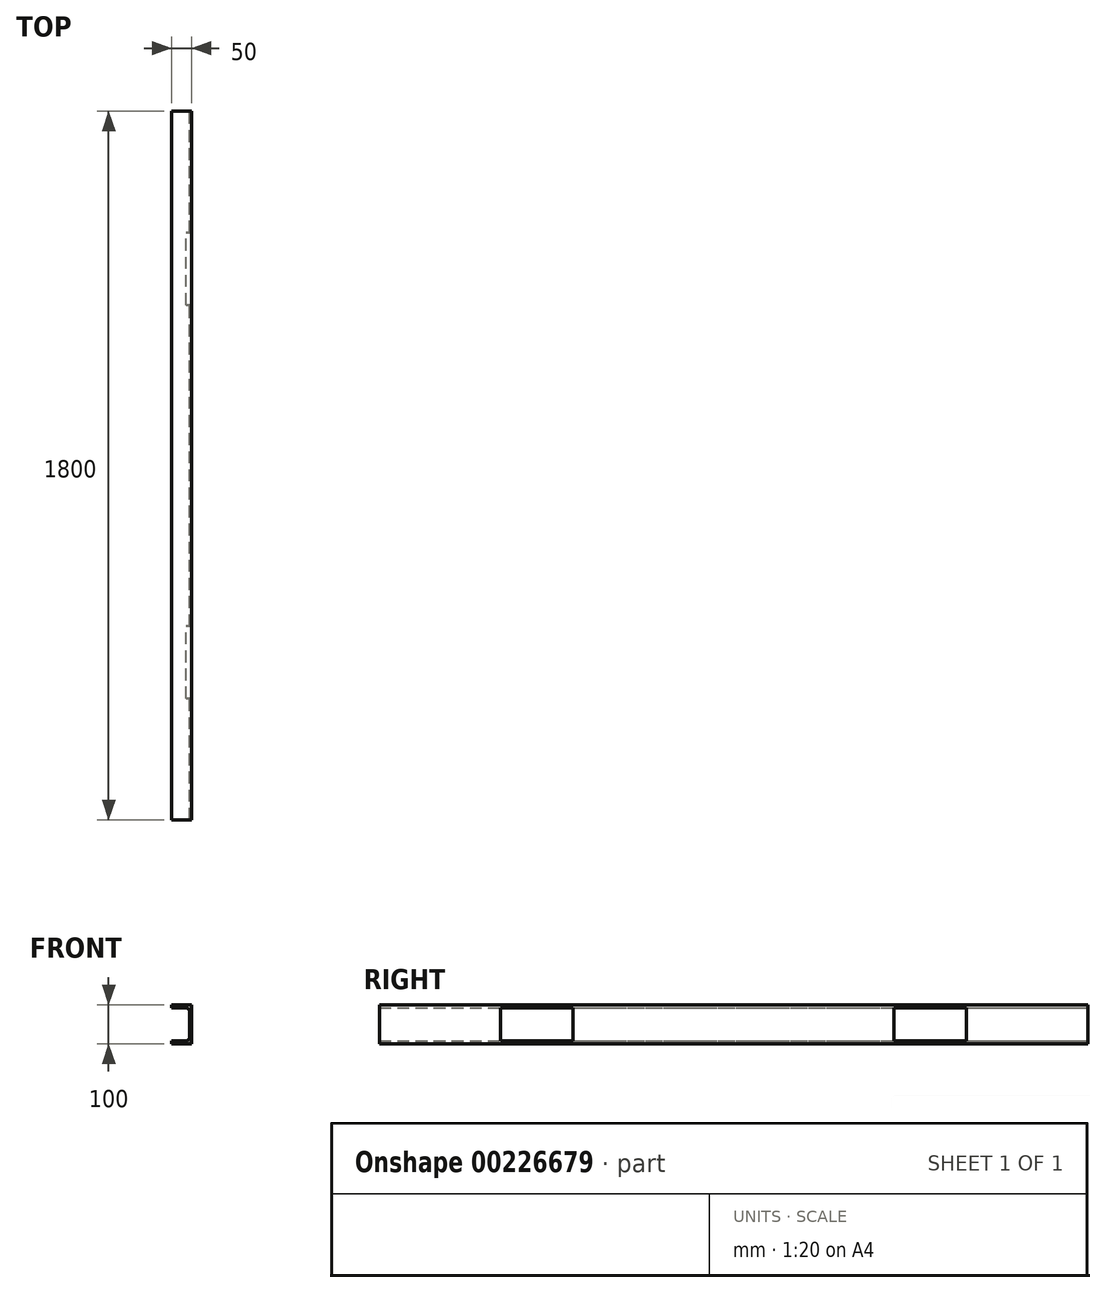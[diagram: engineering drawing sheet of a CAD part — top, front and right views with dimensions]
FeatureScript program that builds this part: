
annotation { "Feature Type Name" : "Feature", "Feature Type Description" : "" }
export const myFeature = defineFeature(function(context is Context, id is Id, definition is map)
    precondition{}
    {
        {
            var Q0;
            Q0=qCreatedBy(makeId("Front.planeOp"),FACE);
            var sketch = newSketch(context, id + "F0", { "sketchPlane" : qUnion([Q0])});
            skLineSegment(sketch, "E0", {"start": v(-50, 50) * mm, "end": v(0, 50) * mm});
            skLineSegment(sketch, "E1", {"start": v(0, 50) * mm, "end": v(0, -50) * mm});
            skLineSegment(sketch, "E2", {"start": v(0, -50) * mm, "end": v(-50, -50) * mm});
            skLineSegment(sketch, "E3", {"start": v(-50, -50) * mm, "end": v(-50, -41.5) * mm});
            skLineSegment(sketch, "E4", {"start": v(-50, -41.5) * mm, "end": v(-14, -41.5) * mm});
            skLineSegment(sketch, "E5", {"start": v(-50, 50) * mm, "end": v(-50, 41.5) * mm});
            skLineSegment(sketch, "E6", {"start": v(-50, 41.5) * mm, "end": v(-14, 41.5) * mm});
            skLineSegment(sketch, "E7", {"start": v(-5, 32.5) * mm, "end": v(-5, -32.5) * mm});
            skPoint(sketch, "E8.visualSharp", {"position": v(-5, 41.5) * mm});
            skArc(sketch, "E8.filletArc", {"start": v(-5, 32.5) * mm, "mid": v(-7.64, 38.86) * mm, "end": v(-14, 41.5) * mm});
            skPoint(sketch, "E9.visualSharp", {"position": v(-5, -41.5) * mm});
            skArc(sketch, "E9.filletArc", {"start": v(-14, -41.5) * mm, "mid": v(-7.64, -38.86) * mm, "end": v(-5, -32.5) * mm});
            skSolve(sketch);
        }
        {
            var Q0;
            Q0=makeQuery(id+"F0.imprint","IMPRINT",FACE,{"disambiguationData":[TD([[makeQuery(id+"F0.imprint","IMPRINT",EDGE,{"derivedFrom":sQuery(id+"F0.wireOp",EDGE,"E0")}),-1.0]])]});
            extrude(context, id + "F1", {"entities" : qUnion([Q0]), "depth" : 1800 * mm});
        }
        {
            var Q0;
            Q0=qCreatedBy(makeId("Right.planeOp"),FACE);
            var sketch = newSketch(context, id + "F2", { "sketchPlane" : qUnion([Q0])});
            skLineSegment(sketch, "E10.top", {"start": v(-308, 42) * mm, "end": v(-461.92, 42) * mm});
            skLineSegment(sketch, "E10.left", {"start": v(-308, 0) * mm, "end": v(-308, 42) * mm});
            skLineSegment(sketch, "E11.bottom", {"start": v(-308, 42) * mm, "end": v(-492, 42) * mm});
            skLineSegment(sketch, "E11.top", {"start": v(-308, -42) * mm, "end": v(-492, -42) * mm});
            skLineSegment(sketch, "E11.left", {"start": v(-308, 42) * mm, "end": v(-308, -42) * mm});
            skLineSegment(sketch, "E11.right", {"start": v(-492, 42) * mm, "end": v(-492, -42) * mm});
            skLineSegment(sketch, "E12.bottom", {"start": v(-1308, 42) * mm, "end": v(-1492, 42) * mm});
            skLineSegment(sketch, "E12.top", {"start": v(-1308, -42) * mm, "end": v(-1492, -42) * mm});
            skLineSegment(sketch, "E12.left", {"start": v(-1308, 42) * mm, "end": v(-1308, -42) * mm});
            skLineSegment(sketch, "E12.right", {"start": v(-1492, 42) * mm, "end": v(-1492, -42) * mm});
            skSolve(sketch);
        }
        {
            var Q0;
            {var subQ4=sQuery(id+"F2.wireOp",EDGE,"E11.top");Q0=makeQuery(id+"F2.imprint","IMPRINT",FACE,{"disambiguationData":[TD([[makeQuery(id+"F2.imprint","IMPRINT",EDGE,{"derivedFrom":subQ4}),-1.0]])]});}
            var Q1;
            Q1=makeQuery(id+"F2.imprint","IMPRINT",FACE,{"disambiguationData":[TD([[makeQuery(id+"F2.imprint","IMPRINT",EDGE,{"derivedFrom":sQuery(id+"F2.wireOp",EDGE,"E12.bottom")}),1.0]])]});
            extrude(context, id + "F3", {"entities" : qUnion([Q0, Q1]), "operationType" : NewBodyOperationType.REMOVE, "oppositeDirection" : true, "depth" : 14 * mm});
        }
    });
